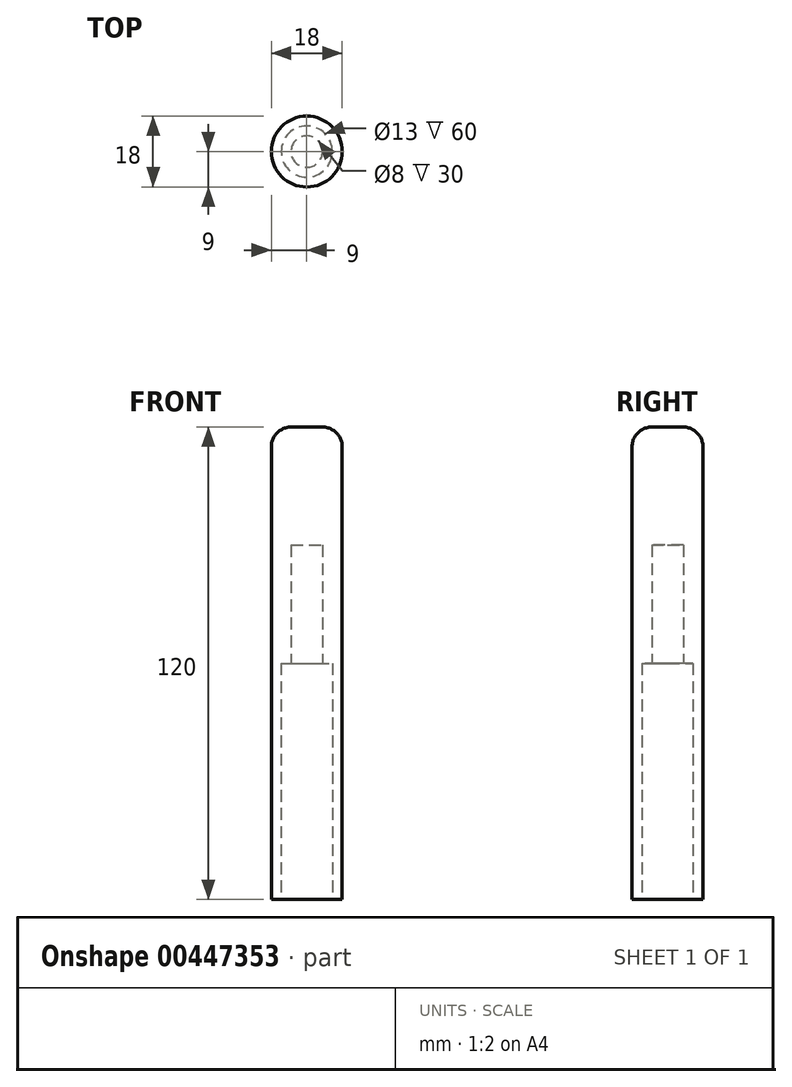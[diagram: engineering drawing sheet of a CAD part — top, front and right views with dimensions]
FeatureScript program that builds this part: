
annotation { "Feature Type Name" : "Feature", "Feature Type Description" : "" }
export const myFeature = defineFeature(function(context is Context, id is Id, definition is map)
    precondition{}
    {
        {
            var Q0;
            Q0=qCreatedBy(makeId("Top.planeOp"),FACE);
            var sketch = newSketch(context, id + "F0", { "sketchPlane" : qUnion([Q0])});
            skCircle(sketch, "E0", {"center": v(0, 0) * mm, "radius": 9 * mm});
            skSolve(sketch);
        }
        {
            var Q0;
            Q0 = qSketchRegion(id + "F0", true);
            extrude(context, id + "F1", {"entities" : qUnion([Q0]), "depth" : 120 * mm});
        }
        {
            var Q0;
            Q0=makeQuery(id+"F1.opExtrude","CAP_FACE",FACE,{"disambiguationData":[OSD([sQuery(id+"F0.wireOp",EDGE,"E0")])],"isStart":true});
            var sketch = newSketch(context, id + "F2", { "sketchPlane" : qUnion([Q0])});
            skCircle(sketch, "E1", {"center": v(0, 0) * mm, "radius": 6.5 * mm});
            skSolve(sketch);
        }
        {
            var Q0;
            Q0=makeQuery(id+"F2.imprint","IMPRINT",FACE,{"disambiguationData":[TD([[makeQuery(id+"F2.imprint","IMPRINT",EDGE,{"derivedFrom":sQuery(id+"F2.wireOp",EDGE,"E1")}),1.0]])]});
            extrude(context, id + "F3", {"entities" : qUnion([Q0]), "operationType" : NewBodyOperationType.REMOVE, "oppositeDirection" : true, "depth" : 60 * mm});
        }
        {
            var Q0;
            Q0=makeQuery(id+"F3.boolean.opBoolean","COPY",FACE,{"derivedFrom":makeQuery(id+"F3.opExtrude","CAP_FACE",FACE,{"disambiguationData":[OSD([sQuery(id+"F2.wireOp",EDGE,"E1")])],"isStart":false})});
            var sketch = newSketch(context, id + "F4", { "sketchPlane" : qUnion([Q0])});
            skCircle(sketch, "E2", {"center": v(0, 0) * mm, "radius": 4 * mm});
            skSolve(sketch);
        }
        {
            var Q0;
            Q0 = qSketchRegion(id + "F4", true);
            extrude(context, id + "F5", {"entities" : qUnion([Q0]), "operationType" : NewBodyOperationType.REMOVE, "oppositeDirection" : true, "depth" : 30 * mm});
        }
        {
            var Q0;
            Q0=makeQuery(id+"F1.opExtrude","CAP_FACE",FACE,{"disambiguationData":[OSD([sQuery(id+"F0.wireOp",EDGE,"E0")])],"isStart":false});
            fillet(context, id + "F6", {"entities" : qUnion([Q0]), "radius" : 5 * mm, "tangentPropagation" : true, "allowEdgeOverflow" : false});
        }
    });
